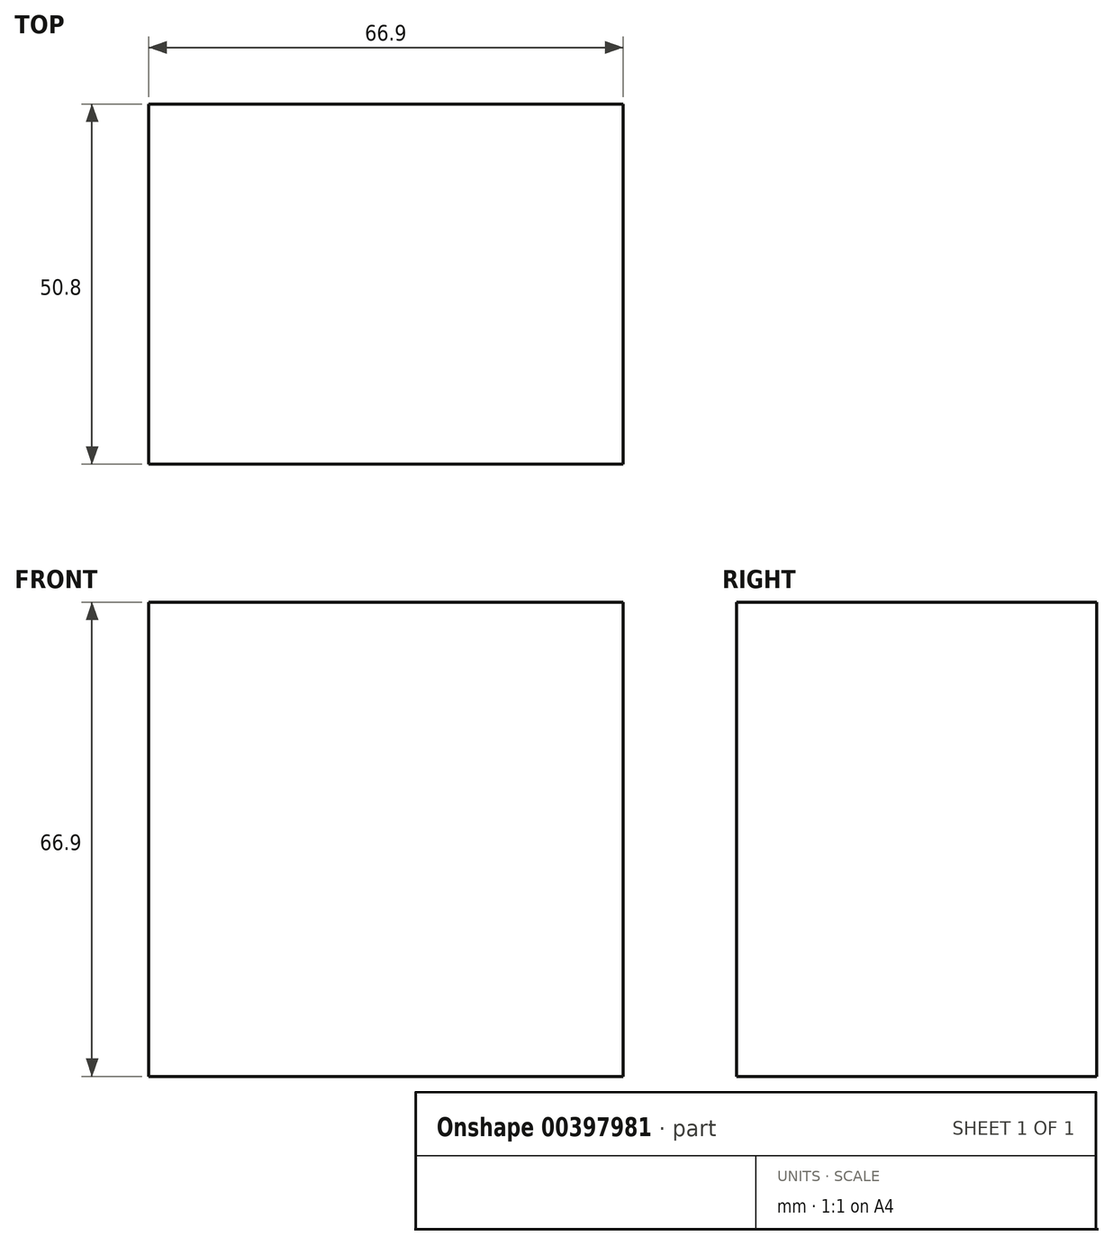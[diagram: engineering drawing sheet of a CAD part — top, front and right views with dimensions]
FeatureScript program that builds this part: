
annotation { "Feature Type Name" : "Feature", "Feature Type Description" : "" }
export const myFeature = defineFeature(function(context is Context, id is Id, definition is map)
    precondition{}
    {
        {
            var Q0;
            Q0=qCreatedBy(makeId("Front.planeOp"),FACE);
            var sketch = newSketch(context, id + "F0", { "sketchPlane" : qUnion([Q0])});
            skLineSegment(sketch, "E0.bottom", {"start": v(33.45, 33.45) * mm, "end": v(-33.45, 33.45) * mm});
            skLineSegment(sketch, "E0.top", {"start": v(33.45, -33.45) * mm, "end": v(-33.45, -33.45) * mm});
            skLineSegment(sketch, "E0.left", {"start": v(33.45, 33.45) * mm, "end": v(33.45, -33.45) * mm});
            skLineSegment(sketch, "E0.right", {"start": v(-33.45, 33.45) * mm, "end": v(-33.45, -33.45) * mm});
            skPoint(sketch, "E0.middle", {"position": v(0, 0) * mm});
            skSolve(sketch);
        }
        {
            var Q0;
            Q0=makeQuery(id+"F0.imprint","IMPRINT",FACE,{"disambiguationData":[TD([[makeQuery(id+"F0.imprint","IMPRINT",EDGE,{"derivedFrom":sQuery(id+"F0.wireOp",EDGE,"E0.bottom")}),1.0]])]});
            extrude(context, id + "F1", {"entities" : qUnion([Q0]), "endBound" : BoundingType.SYMMETRIC, "depth" : 50.8 * mm});
        }
    });
